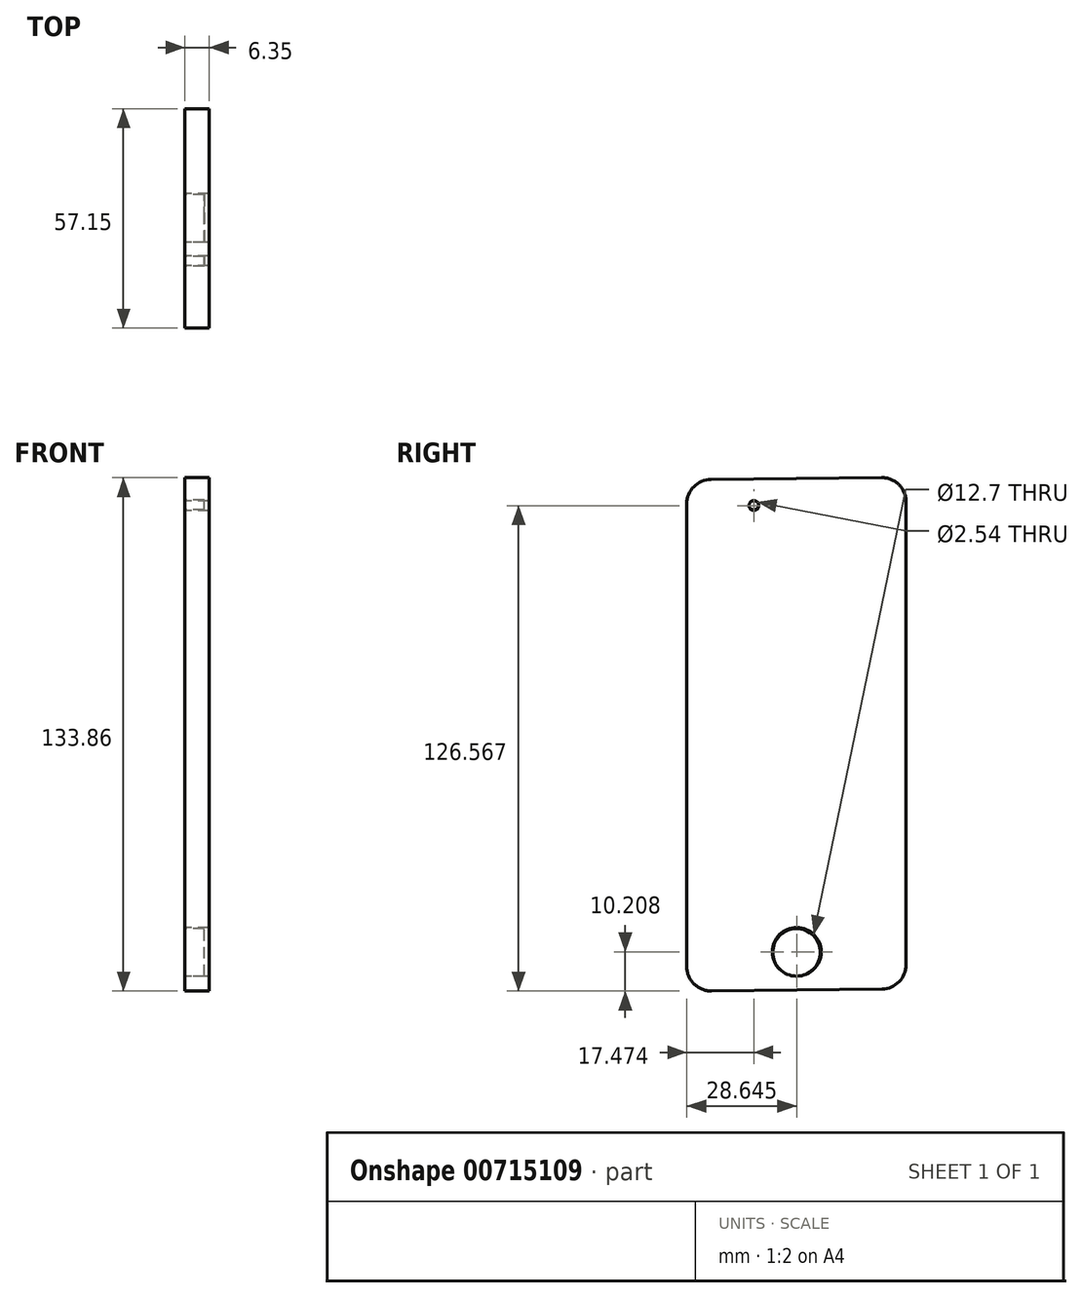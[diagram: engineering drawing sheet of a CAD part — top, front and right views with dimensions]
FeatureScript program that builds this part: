
annotation { "Feature Type Name" : "Feature", "Feature Type Description" : "" }
export const myFeature = defineFeature(function(context is Context, id is Id, definition is map)
    precondition{}
    {
        {
            var Q0;
            Q0=qCreatedBy(makeId("Right.planeOp"),FACE);
            var sketch = newSketch(context, id + "F0", { "sketchPlane" : qUnion([Q0])});
            skLineSegment(sketch, "E0", {"start": v(17.29, 43.52) * mm, "end": v(17.29, -77.13) * mm});
            skLineSegment(sketch, "E1", {"start": v(-39.86, 43.01) * mm, "end": v(-39.86, -77.64) * mm});
            skLineSegment(sketch, "E2", {"start": v(-33.44, -83.98) * mm, "end": v(11, -83.48) * mm});
            skLineSegment(sketch, "E3", {"start": v(10.86, 49.87) * mm, "end": v(-33.58, 49.36) * mm});
            skPoint(sketch, "E4.visualSharp", {"position": v(17.29, 49.95) * mm});
            skArc(sketch, "E4.filletArc", {"start": v(17.29, 43.52) * mm, "mid": v(15.4, 48.04) * mm, "end": v(10.86, 49.87) * mm});
            skPoint(sketch, "E5.visualSharp", {"position": v(-39.86, 49.3) * mm});
            skArc(sketch, "E5.filletArc", {"start": v(-33.58, 49.36) * mm, "mid": v(-38.03, 47.48) * mm, "end": v(-39.86, 43.01) * mm});
            skPoint(sketch, "E6.visualSharp", {"position": v(-39.86, -84.06) * mm});
            skArc(sketch, "E6.filletArc", {"start": v(-39.86, -77.64) * mm, "mid": v(-37.98, -82.15) * mm, "end": v(-33.44, -83.98) * mm});
            skPoint(sketch, "E7.visualSharp", {"position": v(17.29, -83.4) * mm});
            skArc(sketch, "E7.filletArc", {"start": v(11, -83.48) * mm, "mid": v(15.45, -81.6) * mm, "end": v(17.29, -77.13) * mm});
            skCircle(sketch, "E8", {"center": v(-11.22, -73.78) * mm, "radius": 6.35 * mm});
            skPoint(sketch, "E8.centerSnap0", {"position": v(-11.22, -83.73) * mm});
            skLineSegment(sketch, "E9", {"start": v(-11.36, 42.58) * mm, "end": v(-5.01, 42.65) * mm});
            skPoint(sketch, "E9.startSnap0", {"position": v(-11.36, 49.62) * mm});
            skLineSegment(sketch, "E10", {"start": v(-11.36, 42.58) * mm, "end": v(-17.7, 42.5) * mm});
            skCircle(sketch, "E11", {"center": v(-22.39, 42.58) * mm, "radius": 1.27 * mm});
            skSolve(sketch);
        }
        {
            var Q0;
            Q0=makeQuery(id+"F0.imprint","IMPRINT",FACE,{"disambiguationData":[TD([[makeQuery(id+"F0.imprint","IMPRINT",EDGE,{"derivedFrom":sQuery(id+"F0.wireOp",EDGE,"E0")}),-1.0]])]});
            extrude(context, id + "F1", {"entities" : qUnion([Q0]), "depth" : 6.35 * mm, "offsetDistance" : 25.4 * mm});
        }
        {
            var Q0;
            Q0=qCreatedBy(makeId("Right.planeOp"),FACE);
            var sketch = newSketch(context, id + "F2", { "sketchPlane" : qUnion([Q0])});
            skCircle(sketch, "E12", {"center": v(-11.28, -73.93) * mm, "radius": 6.18 * mm});
            skCircle(sketch, "E13", {"center": v(-22.42, 42.75) * mm, "radius": 1.27 * mm});
            skSolve(sketch);
        }
        {
            var Q0;
            Q0 = qSketchRegion(id + "F2", true);
            extrude(context, id + "F3", {"entities" : qUnion([Q0]), "depth" : 5.08 * mm, "offsetDistance" : 25.4 * mm});
        }
        {
            var Q0;
            Q0=qCreatedBy(makeId("Front.planeOp"),FACE);
            var sketch = newSketch(context, id + "F4", { "sketchPlane" : qUnion([Q0])});
            skLineSegment(sketch, "E14.bottom", {"start": v(2.38, 28.4) * mm, "end": v(3.97, 28.4) * mm});
            skLineSegment(sketch, "E14.top", {"start": v(2.38, 22.06) * mm, "end": v(3.97, 22.06) * mm});
            skLineSegment(sketch, "E14.left", {"start": v(2.38, 28.4) * mm, "end": v(2.38, 22.06) * mm});
            skLineSegment(sketch, "E14.right", {"start": v(3.97, 28.4) * mm, "end": v(3.97, 22.06) * mm});
            skLineSegment(sketch, "E15.bottom", {"start": v(2.38, 17.69) * mm, "end": v(3.98, 17.69) * mm});
            skLineSegment(sketch, "E15.top", {"start": v(2.38, 11.34) * mm, "end": v(3.98, 11.34) * mm});
            skLineSegment(sketch, "E15.left", {"start": v(2.38, 17.69) * mm, "end": v(2.38, 11.34) * mm});
            skLineSegment(sketch, "E15.right", {"start": v(3.98, 17.69) * mm, "end": v(3.98, 11.34) * mm});
            skLineSegment(sketch, "E16.bottom", {"start": v(1.92, 40.83) * mm, "end": v(3.52, 40.83) * mm});
            skLineSegment(sketch, "E16.top", {"start": v(1.92, 36.07) * mm, "end": v(3.52, 36.07) * mm});
            skLineSegment(sketch, "E16.left", {"start": v(1.92, 40.83) * mm, "end": v(1.92, 36.07) * mm});
            skLineSegment(sketch, "E16.right", {"start": v(3.52, 40.83) * mm, "end": v(3.52, 36.07) * mm});
            skSolve(sketch);
        }
        {
            var Q0;
            Q0 = qSketchRegion(id + "F4", true);
            extrude(context, id + "F5", {"entities" : qUnion([Q0]), "operationType" : NewBodyOperationType.ADD, "depth" : 1.59 * mm, "offsetDistance" : 25.4 * mm});
        }
    });
